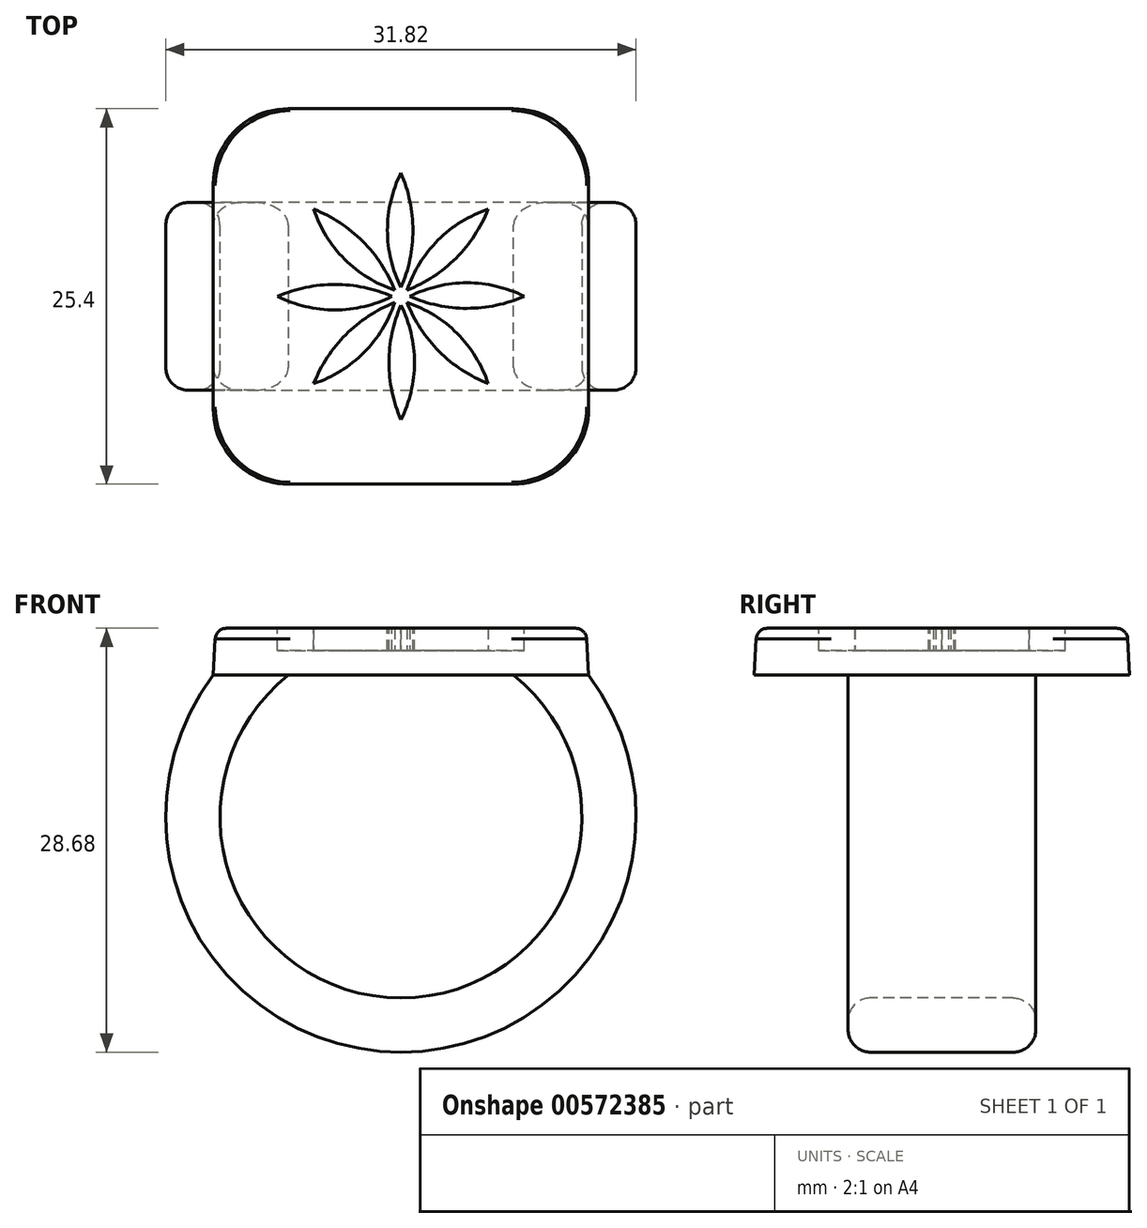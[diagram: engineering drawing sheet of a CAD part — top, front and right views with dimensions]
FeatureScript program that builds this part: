
annotation { "Feature Type Name" : "Feature", "Feature Type Description" : "" }
export const myFeature = defineFeature(function(context is Context, id is Id, definition is map)
    precondition{}
    {
        {
            var Q0;
            Q0=qCreatedBy(makeId("Top.planeOp"),FACE);
            var sketch = newSketch(context, id + "F0", { "sketchPlane" : qUnion([Q0])});
            skLineSegment(sketch, "E0.bottom", {"start": v(12.7, 12.7) * mm, "end": v(-12.7, 12.7) * mm});
            skLineSegment(sketch, "E0.top", {"start": v(12.7, -12.7) * mm, "end": v(-12.7, -12.7) * mm});
            skLineSegment(sketch, "E0.left", {"start": v(12.7, 12.7) * mm, "end": v(12.7, -12.7) * mm});
            skLineSegment(sketch, "E0.right", {"start": v(-12.7, 12.7) * mm, "end": v(-12.7, -12.7) * mm});
            skPoint(sketch, "E0.middle", {"position": v(0, 0) * mm});
            skSolve(sketch);
        }
        {
            var Q0;
            Q0=qSketchRegion(id+"F0",true);
            extrude(context, id + "F1", {"entities" : qUnion([Q0]), "depth" : 3.17 * mm, "offsetDistance" : 25.4 * mm, "hasDraft" : true, "draftAngle" : 3 * degree, "draftPullDirection" : true});
        }
        {
            var Q0;
            Q0=qCreatedBy(makeId("Front.planeOp"),FACE);
            var sketch = newSketch(context, id + "F2", { "sketchPlane" : qUnion([Q0])});
            skArc(sketch, "E1", {"start": v(-10.16, 0) * mm, "mid": v(0, -23.56) * mm, "end": v(10.16, 0) * mm});
            skSolve(sketch);
        }
        {
            var Q0;
            Q0=makeQuery(id+"F1.opExtrude","CAP_FACE",FACE,{"disambiguationData":[OSD([sQuery(id+"F0.wireOp",EDGE,"E0.bottom"),sQuery(id+"F0.wireOp",EDGE,"E0.top"),sQuery(id+"F0.wireOp",EDGE,"E0.left"),sQuery(id+"F0.wireOp",EDGE,"E0.right")])],"isStart":true});
            var sketch = newSketch(context, id + "F3", { "sketchPlane" : qUnion([Q0])});
            skLineSegment(sketch, "E2.bottom", {"start": v(-7.62, -6.35) * mm, "end": v(-12.7, -6.35) * mm});
            skLineSegment(sketch, "E2.top", {"start": v(-7.62, 6.35) * mm, "end": v(-12.7, 6.35) * mm});
            skLineSegment(sketch, "E2.left", {"start": v(-7.62, -6.35) * mm, "end": v(-7.62, 6.35) * mm});
            skLineSegment(sketch, "E2.right", {"start": v(-12.7, -6.35) * mm, "end": v(-12.7, 6.35) * mm});
            skPoint(sketch, "E2.middle", {"position": v(-10.16, 0) * mm});
            skSolve(sketch);
        }
        {
            var Q0;
            Q0=qSketchRegion(id+"F3",true);
            var Q1;
            Q1=qConstructionFilter(qBodyType(qCreatedBy(id+"F2",EDGE),BodyType.WIRE),ConstructionObject.NO);
            sweep(context, id + "F4", {"operationType" : NewBodyOperationType.ADD, "profiles" : qUnion([Q0]), "path" : qUnion([Q1])});
        }
        {
            var Q0;
            Q0=qCreatedBy(makeId("Front.planeOp"),FACE);
            var sketch = newSketch(context, id + "F5", { "sketchPlane" : qUnion([Q0])});
            skLineSegment(sketch, "E3.0", {"start": v(10.16, 0) * mm, "end": v(7.62, 0) * mm});
            skLineSegment(sketch, "E3.1", {"start": v(10.01, -2.54) * mm, "end": v(10.16, 0) * mm});
            skArc(sketch, "E3.2", {"start": v(10.01, -2.54) * mm, "mid": v(8.9, -1.18) * mm, "end": v(7.62, 0) * mm});
            skPoint(sketch, "E4.orphan", {"position": v(12.7, 0) * mm});
            skPoint(sketch, "E5.trimOffspring.end.orphan", {"position": v(-12.7, 0) * mm});
            skPoint(sketch, "E5.trimOffspring.start.orphan", {"position": v(-7.62, 0) * mm});
            skSolve(sketch);
        }
        {
            var Q0;
            Q0=qSketchRegion(id+"F5",true);
            var Q1;
            Q1=makeQuery(id+"F4.opSweep","SWEPT_FACE",FACE,{"disambiguationData":[OSD([sQuery(id+"F2.wireOp",EDGE,"E1"),sQuery(id+"F3.wireOp",EDGE,"E2.top")])]});
            var Q2;
            Q2=makeQuery(id+"F4.opSweep","SWEPT_FACE",FACE,{"disambiguationData":[OSD([sQuery(id+"F2.wireOp",EDGE,"E1"),sQuery(id+"F3.wireOp",EDGE,"E2.bottom")])]});
            extrude(context, id + "F6", {"entities" : qUnion([Q0]), "operationType" : NewBodyOperationType.ADD, "endBound" : BoundingType.UP_TO_SURFACE, "depth" : 25.4 * mm, "endBoundEntityFace" : qUnion([Q1]), "offsetDistance" : 25.4 * mm, "hasSecondDirection" : true, "secondDirectionBound" : SecondDirectionBoundingType.UP_TO_SURFACE, "secondDirectionOppositeDirection" : true, "secondDirectionDepth" : 25.4 * mm, "secondDirectionBoundEntityFace" : qUnion([Q2])});
        }
        {
            var Q0;
            Q0=makeQuery(id+"F1.opExtrude","SWEPT_EDGE",EDGE,{"disambiguationData":[OSD([sQuery(id+"F0.wireOp",EDGE,"E0.bottom"),sQuery(id+"F0.wireOp",EDGE,"E0.right")])]});
            var Q1;
            Q1=makeQuery(id+"F1.opExtrude","SWEPT_EDGE",EDGE,{"disambiguationData":[OSD([sQuery(id+"F0.wireOp",EDGE,"E0.bottom"),sQuery(id+"F0.wireOp",EDGE,"E0.left")])]});
            var Q2;
            Q2=makeQuery(id+"F1.opExtrude","SWEPT_EDGE",EDGE,{"disambiguationData":[OSD([sQuery(id+"F0.wireOp",EDGE,"E0.top"),sQuery(id+"F0.wireOp",EDGE,"E0.left")])]});
            var Q3;
            Q3=makeQuery(id+"F1.opExtrude","SWEPT_EDGE",EDGE,{"disambiguationData":[OSD([sQuery(id+"F0.wireOp",EDGE,"E0.top"),sQuery(id+"F0.wireOp",EDGE,"E0.right")])]});
            fillet(context, id + "F7", {"entities" : qUnion([Q0, Q1, Q2, Q3]), "radius" : 5.08 * mm, "tangentPropagation" : true, "allowEdgeOverflow" : false});
        }
        {
            var Q0;
            {var subQ0=sQuery(id+"F3.wireOp",EDGE,"E2.top");var subQ1=sQuery(id+"F2.wireOp",EDGE,"E1");Q0=makeQuery(id+"F6.boolean.opBoolean","MERGE",EDGE,{"derivedFrom":[makeQuery(id+"F4.opSweep","SWEPT_EDGE",EDGE,{"disambiguationData":[OSD([subQ1,subQ0,sQuery(id+"F3.wireOp",EDGE,"E2.left")])]}),makeQuery(id+"F6.opExtrude","TWEAK_EDGE",EDGE,{"derivedFrom":[makeQuery(id+"F4.opSweep","SWEPT_FACE",FACE,{"disambiguationData":[OSD([subQ1,subQ0])]}),makeQuery(id+"F5.imprint","IMPRINT",EDGE,{"derivedFrom":sQuery(id+"F5.wireOp",EDGE,"E3.2")})]})]});}
            var Q1;
            Q1=makeQuery(id+"F4.opSweep","SWEPT_EDGE",EDGE,{"disambiguationData":[OSD([sQuery(id+"F0.wireOp",EDGE,"E0.right"),sQuery(id+"F2.wireOp",EDGE,"E1"),sQuery(id+"F3.wireOp",EDGE,"E2.top"),sQuery(id+"F3.wireOp",EDGE,"E2.right")])]});
            var Q2;
            Q2=makeQuery(id+"F4.opSweep","SWEPT_EDGE",EDGE,{"disambiguationData":[OSD([sQuery(id+"F0.wireOp",EDGE,"E0.right"),sQuery(id+"F2.wireOp",EDGE,"E1"),sQuery(id+"F3.wireOp",EDGE,"E2.bottom"),sQuery(id+"F3.wireOp",EDGE,"E2.right")])]});
            var Q3;
            {var subQ0=sQuery(id+"F3.wireOp",EDGE,"E2.bottom");var subQ1=sQuery(id+"F2.wireOp",EDGE,"E1");Q3=makeQuery(id+"F6.boolean.opBoolean","MERGE",EDGE,{"derivedFrom":[makeQuery(id+"F4.opSweep","SWEPT_EDGE",EDGE,{"disambiguationData":[OSD([subQ1,subQ0,sQuery(id+"F3.wireOp",EDGE,"E2.left")])]}),makeQuery(id+"F6.opExtrude","TWEAK_EDGE",EDGE,{"derivedFrom":[makeQuery(id+"F4.opSweep","SWEPT_FACE",FACE,{"disambiguationData":[OSD([subQ1,subQ0])]}),makeQuery(id+"F5.imprint","IMPRINT",EDGE,{"derivedFrom":sQuery(id+"F5.wireOp",EDGE,"E3.2")})]})]});}
            fillet(context, id + "F8", {"entities" : qUnion([Q0, Q1, Q2, Q3]), "radius" : 1.52 * mm, "tangentPropagation" : true, "allowEdgeOverflow" : false});
        }
        {
            var Q0;
            Q0=makeQuery(id+"F1.opExtrude","CAP_FACE",FACE,{"disambiguationData":[OSD([sQuery(id+"F0.wireOp",EDGE,"E0.bottom"),sQuery(id+"F0.wireOp",EDGE,"E0.top"),sQuery(id+"F0.wireOp",EDGE,"E0.left"),sQuery(id+"F0.wireOp",EDGE,"E0.right")])],"isStart":false});
            fillet(context, id + "F9", {"entities" : qUnion([Q0]), "radius" : 0.76 * mm, "tangentPropagation" : true, "allowEdgeOverflow" : false});
        }
        {
            var Q0;
            Q0=makeQuery(id+"F1.opExtrude","CAP_FACE",FACE,{"disambiguationData":[OSD([sQuery(id+"F0.wireOp",EDGE,"E0.bottom"),sQuery(id+"F0.wireOp",EDGE,"E0.top"),sQuery(id+"F0.wireOp",EDGE,"E0.left"),sQuery(id+"F0.wireOp",EDGE,"E0.right")])],"isStart":false});
            var sketch = newSketch(context, id + "F10", { "sketchPlane" : qUnion([Q0])});
            skCircle(sketch, "E6", {"center": v(0, 0) * mm, "radius": 0.6 * mm});
            skArc(sketch, "E7", {"start": v(0, 0.6) * mm, "mid": v(0.6, 2.5) * mm, "end": v(0.8, 4.47) * mm});
            skArc(sketch, "E8", {"start": v(0.8, 4.47) * mm, "mid": v(0.6, 6.45) * mm, "end": v(0, 8.34) * mm});
            skArc(sketch, "E9", {"start": v(0, 8.34) * mm, "mid": v(-0.68, 6.46) * mm, "end": v(-0.92, 4.47) * mm});
            skArc(sketch, "E10", {"start": v(-0.92, 4.47) * mm, "mid": v(-0.68, 2.48) * mm, "end": v(0, 0.6) * mm});
            skArc(sketch, "E11", {"start": v(-0.42, 0.42) * mm, "mid": v(-1.34, 2.19) * mm, "end": v(-2.6, 3.73) * mm});
            skArc(sketch, "E12", {"start": v(-2.6, 3.73) * mm, "mid": v(-4.13, 4.98) * mm, "end": v(-5.9, 5.9) * mm});
            skArc(sketch, "E13", {"start": v(-5.9, 5.9) * mm, "mid": v(-5.05, 4.08) * mm, "end": v(-3.8, 2.51) * mm});
            skArc(sketch, "E14", {"start": v(-3.8, 2.51) * mm, "mid": v(-2.24, 1.27) * mm, "end": v(-0.42, 0.42) * mm});
            skArc(sketch, "E15", {"start": v(-0.6, 0) * mm, "mid": v(-2.5, 0.6) * mm, "end": v(-4.47, 0.8) * mm});
            skArc(sketch, "E16", {"start": v(-4.47, 0.8) * mm, "mid": v(-6.45, 0.6) * mm, "end": v(-8.34, 0) * mm});
            skArc(sketch, "E17", {"start": v(-8.34, 0) * mm, "mid": v(-6.46, -0.68) * mm, "end": v(-4.47, -0.92) * mm});
            skArc(sketch, "E18", {"start": v(-4.47, -0.92) * mm, "mid": v(-2.48, -0.68) * mm, "end": v(-0.6, 0) * mm});
            skArc(sketch, "E19", {"start": v(-0.42, -0.42) * mm, "mid": v(-2.19, -1.34) * mm, "end": v(-3.73, -2.59) * mm});
            skArc(sketch, "E20", {"start": v(-3.73, -2.59) * mm, "mid": v(-4.98, -4.13) * mm, "end": v(-5.9, -5.9) * mm});
            skArc(sketch, "E21", {"start": v(-5.9, -5.9) * mm, "mid": v(-4.08, -5.05) * mm, "end": v(-2.51, -3.8) * mm});
            skArc(sketch, "E22", {"start": v(-2.51, -3.8) * mm, "mid": v(-1.27, -2.24) * mm, "end": v(-0.42, -0.42) * mm});
            skArc(sketch, "E23", {"start": v(0, -0.6) * mm, "mid": v(-0.6, -2.5) * mm, "end": v(-0.8, -4.47) * mm});
            skArc(sketch, "E24", {"start": v(-0.8, -4.47) * mm, "mid": v(-0.6, -6.45) * mm, "end": v(0, -8.34) * mm});
            skArc(sketch, "E25", {"start": v(0, -8.34) * mm, "mid": v(0.68, -6.46) * mm, "end": v(0.92, -4.47) * mm});
            skArc(sketch, "E26", {"start": v(0.92, -4.47) * mm, "mid": v(0.68, -2.48) * mm, "end": v(0, -0.6) * mm});
            skArc(sketch, "E27", {"start": v(0.42, -0.42) * mm, "mid": v(1.34, -2.19) * mm, "end": v(2.59, -3.73) * mm});
            skArc(sketch, "E28", {"start": v(2.59, -3.73) * mm, "mid": v(4.13, -4.98) * mm, "end": v(5.9, -5.9) * mm});
            skArc(sketch, "E29", {"start": v(5.9, -5.9) * mm, "mid": v(5.05, -4.08) * mm, "end": v(3.8, -2.51) * mm});
            skArc(sketch, "E30", {"start": v(3.8, -2.51) * mm, "mid": v(2.24, -1.27) * mm, "end": v(0.42, -0.42) * mm});
            skArc(sketch, "E31", {"start": v(0.6, 0) * mm, "mid": v(2.5, -0.6) * mm, "end": v(4.47, -0.8) * mm});
            skArc(sketch, "E32", {"start": v(4.47, -0.8) * mm, "mid": v(6.45, -0.6) * mm, "end": v(8.34, 0) * mm});
            skArc(sketch, "E33", {"start": v(8.34, 0) * mm, "mid": v(6.46, 0.68) * mm, "end": v(4.47, 0.92) * mm});
            skArc(sketch, "E34", {"start": v(4.47, 0.92) * mm, "mid": v(2.48, 0.68) * mm, "end": v(0.6, 0) * mm});
            skArc(sketch, "E35", {"start": v(0.42, 0.42) * mm, "mid": v(2.19, 1.34) * mm, "end": v(3.73, 2.6) * mm});
            skArc(sketch, "E36", {"start": v(3.73, 2.6) * mm, "mid": v(4.98, 4.13) * mm, "end": v(5.9, 5.9) * mm});
            skArc(sketch, "E37", {"start": v(5.9, 5.9) * mm, "mid": v(4.08, 5.05) * mm, "end": v(2.51, 3.8) * mm});
            skArc(sketch, "E38", {"start": v(2.51, 3.8) * mm, "mid": v(1.27, 2.24) * mm, "end": v(0.42, 0.42) * mm});
            skSolve(sketch);
        }
        {
            var Q0;
            Q0=makeQuery(id+"F10.imprint","IMPRINT",FACE,{"disambiguationData":[TD([[makeQuery(id+"F10.imprint","IMPRINT",EDGE,{"derivedFrom":sQuery(id+"F10.wireOp",EDGE,"E7")}),1.0]])]});
            var Q1;
            Q1=makeQuery(id+"F10.imprint","IMPRINT",FACE,{"disambiguationData":[TD([[makeQuery(id+"F10.imprint","IMPRINT",EDGE,{"derivedFrom":sQuery(id+"F10.wireOp",EDGE,"E11")}),1.0]])]});
            var Q2;
            Q2=makeQuery(id+"F10.imprint","IMPRINT",FACE,{"disambiguationData":[TD([[makeQuery(id+"F10.imprint","IMPRINT",EDGE,{"derivedFrom":sQuery(id+"F10.wireOp",EDGE,"E15")}),1.0]])]});
            var Q3;
            Q3=makeQuery(id+"F10.imprint","IMPRINT",FACE,{"disambiguationData":[TD([[makeQuery(id+"F10.imprint","IMPRINT",EDGE,{"derivedFrom":sQuery(id+"F10.wireOp",EDGE,"E19")}),1.0]])]});
            var Q4;
            Q4=makeQuery(id+"F10.imprint","IMPRINT",FACE,{"disambiguationData":[TD([[makeQuery(id+"F10.imprint","IMPRINT",EDGE,{"derivedFrom":sQuery(id+"F10.wireOp",EDGE,"E23")}),1.0]])]});
            var Q5;
            Q5=makeQuery(id+"F10.imprint","IMPRINT",FACE,{"disambiguationData":[TD([[makeQuery(id+"F10.imprint","IMPRINT",EDGE,{"derivedFrom":sQuery(id+"F10.wireOp",EDGE,"E27")}),1.0]])]});
            var Q6;
            Q6=makeQuery(id+"F10.imprint","IMPRINT",FACE,{"disambiguationData":[TD([[makeQuery(id+"F10.imprint","IMPRINT",EDGE,{"derivedFrom":sQuery(id+"F10.wireOp",EDGE,"E31")}),1.0]])]});
            var Q7;
            Q7=makeQuery(id+"F10.imprint","IMPRINT",FACE,{"disambiguationData":[TD([[makeQuery(id+"F10.imprint","IMPRINT",EDGE,{"derivedFrom":sQuery(id+"F10.wireOp",EDGE,"E35")}),1.0]])]});
            extrude(context, id + "F11", {"entities" : qUnion([Q0, Q1, Q2, Q3, Q4, Q5, Q6, Q7]), "operationType" : NewBodyOperationType.REMOVE, "oppositeDirection" : true, "depth" : 1.52 * mm, "offsetDistance" : 25.4 * mm});
        }
    });
